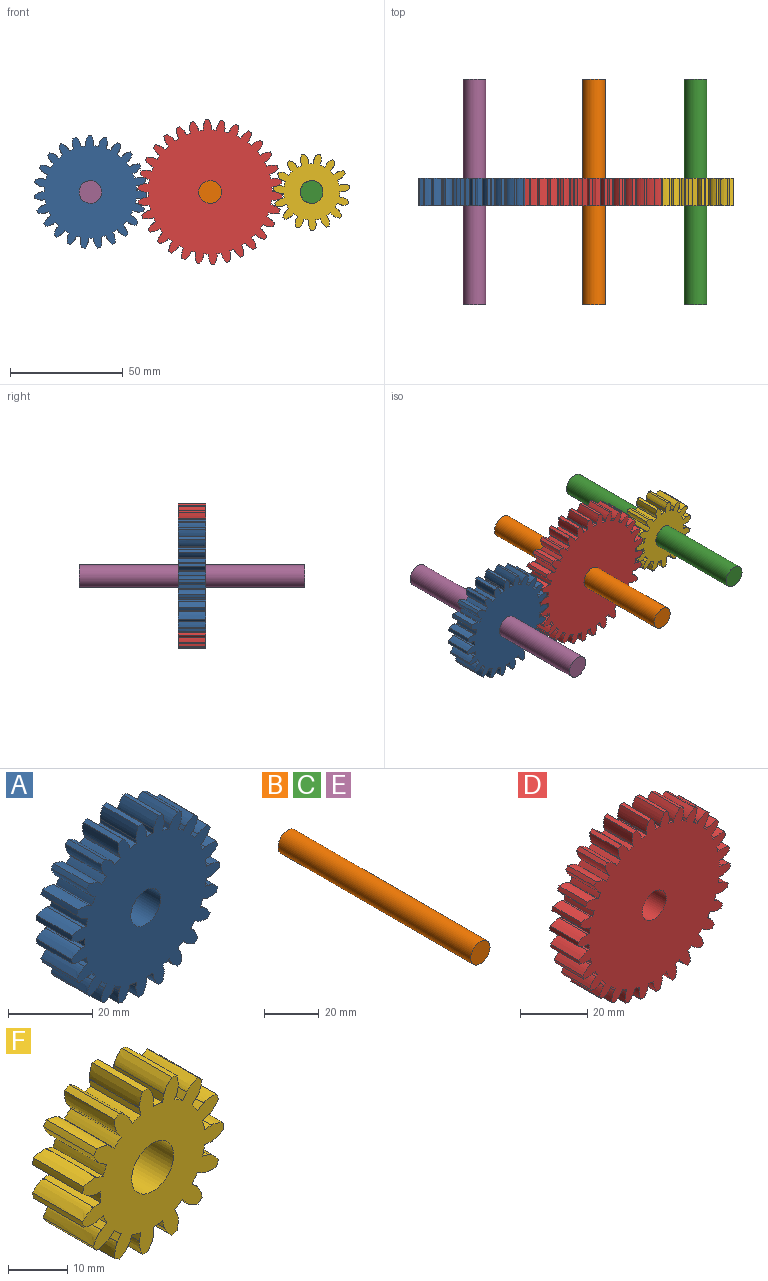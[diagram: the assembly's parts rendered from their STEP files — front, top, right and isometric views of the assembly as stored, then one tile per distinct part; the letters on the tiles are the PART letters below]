
ASSEMBLY  parts=6 mates=6
PART A: 141 faces, bbox 49.9x12x50 mm
  f0: cylinder r=20.5mm len=12mm, axis (0,1,0), area 25.9mm2, adj f23,f24,f26,f137
  f1: cylinder r=20.5mm len=12mm, axis (0,1,0), area 25.9mm2, adj f23,f24,f132,f136
  f2: cylinder r=20.5mm len=12mm, axis (0,1,0), area 25.9mm2, adj f23,f24,f127,f131
  f3: cylinder r=20.5mm len=12mm, axis (0,1,0), area 25.9mm2, adj f23,f24,f122,f126
  f4: cylinder r=20.5mm len=12mm, axis (0,1,0), area 25.9mm2, adj f23,f24,f117,f121
  f5: cylinder r=20.5mm len=12mm, axis (0,1,0), area 25.9mm2, adj f23,f24,f112,f116
  f6: cylinder r=20.5mm len=12mm, axis (0,1,0), area 25.9mm2, adj f23,f24,f107,f111
  f7: cylinder r=20.5mm len=12mm, axis (0,1,0), area 25.9mm2, adj f23,f24,f102,f106
  f8: cylinder r=20.5mm len=12mm, axis (0,1,0), area 25.9mm2, adj f23,f24,f97,f101
  f9: cylinder r=20.5mm len=12mm, axis (0,1,0), area 25.9mm2, adj f23,f24,f92,f96
  f10: cylinder r=20.5mm len=12mm, axis (0,1,0), area 25.9mm2, adj f23,f24,f87,f91
  f11: cylinder r=20.5mm len=12mm, axis (0,1,0), area 25.9mm2, adj f23,f24,f82,f86
  f12: cylinder r=20.5mm len=12mm, axis (0,1,0), area 25.9mm2, adj f23,f24,f77,f81
  f13: cylinder r=20.5mm len=12mm, axis (0,1,0), area 25.9mm2, adj f23,f24,f72,f76
  f14: cylinder r=20.5mm len=12mm, axis (0,1,0), area 25.9mm2, adj f23,f24,f67,f71
  f15: cylinder r=20.5mm len=12mm, axis (0,1,0), area 25.9mm2, adj f23,f24,f62,f66
  f16: cylinder r=20.5mm len=12mm, axis (0,1,0), area 25.9mm2, adj f23,f24,f57,f61
  f17: cylinder r=20.5mm len=12mm, axis (0,1,0), area 25.9mm2, adj f23,f24,f52,f56
  f18: cylinder r=20.5mm len=12mm, axis (0,1,0), area 25.9mm2, adj f23,f24,f47,f51
  f19: cylinder r=20.5mm len=12mm, axis (0,1,0), area 25.9mm2, adj f23,f24,f42,f46
  f20: cylinder r=20.5mm len=12mm, axis (0,1,0), area 25.9mm2, adj f23,f24,f37,f41
  f21: cylinder r=20.5mm len=12mm, axis (0,1,0), area 25.9mm2, adj f23,f24,f32,f36
  f22: cylinder r=20.5mm len=12mm, axis (0,1,0), area 25.9mm2, adj f23,f24,f27,f31
  f23: plane 49.96x49.85mm, normal (0,-1,0), area 1550.3mm2, adj f0,f1,f2,f3,f4,f5,f6,f7
  f24: plane 49.96x49.85mm, normal (0,1,0), area 1550.3mm2, adj f0,f1,f2,f3,f4,f5,f6,f7
  f25: extruded ~12x3.52mm, area 43.8mm2, adj f23,f24,f26,f29
  f26: plane 12x1.1mm, normal (-0.99,0,-0.14), area 13.4mm2, adj f0,f23,f24,f25
  f27: plane 12x1.11mm, normal (1,0,0), area 13.4mm2, adj f22,f23,f24,f28
  f28: extruded ~12x3.37mm, area 43.8mm2, adj f23,f24,f27,f29
  f29: cylinder r=25mm len=12mm, axis (0,1,0), area 17.1mm2, adj f23,f24,f25,f28
  f30: extruded ~12x3.16mm, area 43.8mm2, adj f23,f24,f31,f34
  f31: plane 12x1.1mm, normal (-0.99,0,0.14), area 13.4mm2, adj f22,f23,f24,f30
  f32: plane 12x1.07mm, normal (0.96,0,-0.27), area 13.4mm2, adj f21,f23,f24,f33
  f33: extruded ~12x3.6mm, area 43.8mm2, adj f23,f24,f32,f34
  f34: cylinder r=25mm len=12mm, axis (0,1,0), area 17.1mm2, adj f23,f24,f30,f33
  f35: extruded ~12x2.57mm, area 43.8mm2, adj f23,f24,f36,f39
  f36: plane 12x1.02mm, normal (-0.92,0,0.4), area 13.4mm2, adj f21,f23,f24,f35
  f37: plane 12x0.95mm, normal (0.85,0,-0.52), area 13.4mm2, adj f20,f23,f24,f38
  f38: extruded ~12x3.56mm, area 43.8mm2, adj f23,f24,f37,f39
  f39: cylinder r=25mm len=12mm, axis (0,1,0), area 17.1mm2, adj f23,f24,f35,f38
  f40: extruded ~12x3.15mm, area 43.8mm2, adj f23,f24,f41,f44
  f41: plane 12x0.86mm, normal (-0.78,0,0.63), area 13.4mm2, adj f20,f23,f24,f40
  f42: plane 12x0.81mm, normal (0.68,0,-0.73), area 13.4mm2, adj f19,f23,f24,f43
  f43: extruded ~12x3.26mm, area 43.8mm2, adj f23,f24,f42,f44
  f44: cylinder r=25mm len=12mm, axis (0,1,0), area 17.1mm2, adj f23,f24,f40,f43
  f45: extruded ~12x3.51mm, area 43.8mm2, adj f23,f24,f46,f49
  f46: plane 12x0.91mm, normal (-0.58,0,0.82), area 13.4mm2, adj f19,f23,f24,f45
  f47: plane 12x0.99mm, normal (0.46,0,-0.89), area 13.4mm2, adj f18,f23,f24,f48
  f48: extruded ~12x2.72mm, area 43.8mm2, adj f23,f24,f47,f49
  f49: cylinder r=25mm len=12mm, axis (0,1,0), area 17.1mm2, adj f23,f24,f45,f48
  f50: extruded ~12x3.62mm, area 43.8mm2, adj f23,f24,f51,f54
  f51: plane 12x1.05mm, normal (-0.33,0,0.94), area 13.4mm2, adj f18,f23,f24,f50
  f52: plane 12x1.09mm, normal (0.2,0,-0.98), area 13.4mm2, adj f17,f23,f24,f53
  f53: extruded ~12x3.03mm, area 43.8mm2, adj f23,f24,f52,f54
  f54: cylinder r=25mm len=12mm, axis (0,1,0), area 17.1mm2, adj f23,f24,f50,f53
  f55: extruded ~12x3.45mm, area 43.8mm2, adj f23,f24,f56,f59
  f56: plane 12x1.11mm, normal (-0.07,0,1), area 13.4mm2, adj f17,f23,f24,f55
  f57: plane 12x1.11mm, normal (-0.07,0,-1), area 13.4mm2, adj f16,f23,f24,f58
  f58: extruded ~12x3.45mm, area 43.8mm2, adj f23,f24,f57,f59
  f59: cylinder r=25mm len=12mm, axis (0,1,0), area 17.1mm2, adj f23,f24,f55,f58
  f60: extruded ~12x3.03mm, area 43.8mm2, adj f23,f24,f61,f64
  f61: plane 12x1.09mm, normal (0.2,0,0.98), area 13.4mm2, adj f16,f23,f24,f60
  f62: plane 12x1.05mm, normal (-0.33,0,-0.94), area 13.4mm2, adj f15,f23,f24,f63
  f63: extruded ~12x3.62mm, area 43.8mm2, adj f23,f24,f62,f64
  f64: cylinder r=25mm len=12mm, axis (0,1,0), area 17.1mm2, adj f23,f24,f60,f63
  f65: extruded ~12x2.72mm, area 43.8mm2, adj f23,f24,f66,f69
  f66: plane 12x0.99mm, normal (0.46,0,0.89), area 13.4mm2, adj f15,f23,f24,f65
  f67: plane 12x0.91mm, normal (-0.58,0,-0.82), area 13.4mm2, adj f14,f23,f24,f68
  f68: extruded ~12x3.51mm, area 43.8mm2, adj f23,f24,f67,f69
  f69: cylinder r=25mm len=12mm, axis (0,1,0), area 17.1mm2, adj f23,f24,f65,f68
  f70: extruded ~12x3.26mm, area 43.8mm2, adj f23,f24,f71,f74
  f71: plane 12x0.81mm, normal (0.68,0,0.73), area 13.4mm2, adj f14,f23,f24,f70
  f72: plane 12x0.86mm, normal (-0.78,0,-0.63), area 13.4mm2, adj f13,f23,f24,f73
  f73: extruded ~12x3.15mm, area 43.8mm2, adj f23,f24,f72,f74
  f74: cylinder r=25mm len=12mm, axis (0,1,0), area 17.1mm2, adj f23,f24,f70,f73
  f75: extruded ~12x3.56mm, area 43.8mm2, adj f23,f24,f76,f79
  f76: plane 12x0.95mm, normal (0.85,0,0.52), area 13.4mm2, adj f13,f23,f24,f75
  f77: plane 12x1.02mm, normal (-0.92,0,-0.4), area 13.4mm2, adj f12,f23,f24,f78
  f78: extruded ~12x2.57mm, area 43.8mm2, adj f23,f24,f77,f79
  f79: cylinder r=25mm len=12mm, axis (0,1,0), area 17.1mm2, adj f23,f24,f75,f78
  f80: extruded ~12x3.6mm, area 43.8mm2, adj f23,f24,f81,f84
  f81: plane 12x1.07mm, normal (0.96,0,0.27), area 13.4mm2, adj f12,f23,f24,f80
  f82: plane 12x1.1mm, normal (-0.99,0,-0.14), area 13.4mm2, adj f11,f23,f24,f83
  f83: extruded ~12x3.16mm, area 43.8mm2, adj f23,f24,f82,f84
  f84: cylinder r=25mm len=12mm, axis (0,1,0), area 17.1mm2, adj f23,f24,f80,f83
  f85: extruded ~12x3.37mm, area 43.8mm2, adj f23,f24,f86,f89
  f86: plane 12x1.11mm, normal (1,0,0), area 13.4mm2, adj f11,f23,f24,f85
  f87: plane 12x1.1mm, normal (-0.99,0,0.14), area 13.4mm2, adj f10,f23,f24,f88
  f88: extruded ~12x3.52mm, area 43.8mm2, adj f23,f24,f87,f89
  f89: cylinder r=25mm len=12mm, axis (0,1,0), area 17.1mm2, adj f23,f24,f85,f88
  f90: extruded ~12x2.89mm, area 43.8mm2, adj f23,f24,f91,f94
  f91: plane 12x1.07mm, normal (0.96,0,-0.27), area 13.4mm2, adj f10,f23,f24,f90
  f92: plane 12x1.02mm, normal (-0.92,0,0.4), area 13.4mm2, adj f9,f23,f24,f93
  f93: extruded ~12x3.62mm, area 43.8mm2, adj f23,f24,f92,f94
  f94: cylinder r=25mm len=12mm, axis (0,1,0), area 17.1mm2, adj f23,f24,f90,f93
  f95: extruded ~12x2.88mm, area 43.8mm2, adj f23,f24,f96,f99
  f96: plane 12x0.95mm, normal (0.85,0,-0.52), area 13.4mm2, adj f9,f23,f24,f95
  f97: plane 12x0.86mm, normal (-0.78,0,0.63), area 13.4mm2, adj f8,f23,f24,f98
  f98: extruded ~12x3.45mm, area 43.8mm2, adj f23,f24,f97,f99
  f99: cylinder r=25mm len=12mm, axis (0,1,0), area 17.1mm2, adj f23,f24,f95,f98
  f100: extruded ~12x3.36mm, area 43.8mm2, adj f23,f24,f101,f104
  f101: plane 12x0.81mm, normal (0.68,0,-0.73), area 13.4mm2, adj f8,f23,f24,f100
  f102: plane 12x0.91mm, normal (-0.58,0,0.82), area 13.4mm2, adj f7,f23,f24,f103
  f103: extruded ~12x3.02mm, area 43.8mm2, adj f23,f24,f102,f104
  f104: cylinder r=25mm len=12mm, axis (0,1,0), area 17.1mm2, adj f23,f24,f100,f103
  f105: extruded ~12x3.6mm, area 43.8mm2, adj f23,f24,f106,f109
  f106: plane 12x0.99mm, normal (0.46,0,-0.89), area 13.4mm2, adj f7,f23,f24,f105
  f107: plane 12x1.05mm, normal (-0.33,0,0.94), area 13.4mm2, adj f6,f23,f24,f108
  f108: extruded ~12x2.73mm, area 43.8mm2, adj f23,f24,f107,f109
  f109: cylinder r=25mm len=12mm, axis (0,1,0), area 17.1mm2, adj f23,f24,f105,f108
  f110: extruded ~12x3.57mm, area 43.8mm2, adj f23,f24,f111,f114
  f111: plane 12x1.09mm, normal (0.2,0,-0.98), area 13.4mm2, adj f6,f23,f24,f110
  f112: plane 12x1.11mm, normal (-0.07,0,1), area 13.4mm2, adj f5,f23,f24,f113
  f113: extruded ~12x3.27mm, area 43.8mm2, adj f23,f24,f112,f114
  f114: cylinder r=25mm len=12mm, axis (0,1,0), area 17.1mm2, adj f23,f24,f110,f113
  f115: extruded ~12x3.27mm, area 43.8mm2, adj f23,f24,f116,f119
  f116: plane 12x1.11mm, normal (-0.07,0,-1), area 13.4mm2, adj f5,f23,f24,f115
  f117: plane 12x1.09mm, normal (0.2,0,0.98), area 13.4mm2, adj f4,f23,f24,f118
  f118: extruded ~12x3.57mm, area 43.8mm2, adj f23,f24,f117,f119
  f119: cylinder r=25mm len=12mm, axis (0,1,0), area 17.1mm2, adj f23,f24,f115,f118
  f120: extruded ~12x2.73mm, area 43.8mm2, adj f23,f24,f121,f124
  f121: plane 12x1.05mm, normal (-0.33,0,-0.94), area 13.4mm2, adj f4,f23,f24,f120
  f122: plane 12x0.99mm, normal (0.46,0,0.89), area 13.4mm2, adj f3,f23,f24,f123
  f123: extruded ~12x3.6mm, area 43.8mm2, adj f23,f24,f122,f124
  f124: cylinder r=25mm len=12mm, axis (0,1,0), area 17.1mm2, adj f23,f24,f120,f123
  f125: extruded ~12x3.02mm, area 43.8mm2, adj f23,f24,f126,f129
  f126: plane 12x0.91mm, normal (-0.58,0,-0.82), area 13.4mm2, adj f3,f23,f24,f125
  f127: plane 12x0.81mm, normal (0.68,0,0.73), area 13.4mm2, adj f2,f23,f24,f128
  f128: extruded ~12x3.36mm, area 43.8mm2, adj f23,f24,f127,f129
  f129: cylinder r=25mm len=12mm, axis (0,1,0), area 17.1mm2, adj f23,f24,f125,f128
  f130: extruded ~12x3.45mm, area 43.8mm2, adj f23,f24,f131,f134
  f131: plane 12x0.86mm, normal (-0.78,0,-0.63), area 13.4mm2, adj f2,f23,f24,f130
  f132: plane 12x0.95mm, normal (0.85,0,0.52), area 13.4mm2, adj f1,f23,f24,f133
  f133: extruded ~12x2.88mm, area 43.8mm2, adj f23,f24,f132,f134
  f134: cylinder r=25mm len=12mm, axis (0,1,0), area 17.1mm2, adj f23,f24,f130,f133
  f135: extruded ~12x3.62mm, area 43.8mm2, adj f23,f24,f136,f139
  f136: plane 12x1.02mm, normal (-0.92,0,-0.4), area 13.4mm2, adj f1,f23,f24,f135
  f137: plane 12x1.07mm, normal (0.96,0,0.27), area 13.4mm2, adj f0,f23,f24,f138
  f138: extruded ~12x2.89mm, area 43.8mm2, adj f23,f24,f137,f139
  f139: cylinder r=25mm len=12mm, axis (0,1,0), area 17.1mm2, adj f23,f24,f135,f138
  f140: cylinder r=5mm len=12mm, axis (0,1,0), area 377mm2, adj f23,f24
PART B: 3 faces, bbox 10x100x10 mm
  f0: cylinder r=5mm len=100mm, axis (0,1,0), area 3141.6mm2, adj f1,f2
  f1: plane 10x10mm, normal (0,-1,0), area 78.5mm2, adj f0
  f2: plane 10x10mm, normal (0,1,0), area 78.5mm2, adj f0
PART C: same geometry as B
PART D: 183 faces, bbox 64x12x64 mm
  f0: cylinder r=27.5mm len=12mm, axis (0,1,0), area 24.5mm2, adj f30,f31,f33,f179
  f1: cylinder r=27.5mm len=12mm, axis (0,1,0), area 24.5mm2, adj f30,f31,f174,f178
  f2: cylinder r=27.5mm len=12mm, axis (0,1,0), area 24.5mm2, adj f30,f31,f169,f173
  f3: cylinder r=27.5mm len=12mm, axis (0,1,0), area 24.5mm2, adj f30,f31,f164,f168
  f4: cylinder r=27.5mm len=12mm, axis (0,1,0), area 24.5mm2, adj f30,f31,f159,f163
  f5: cylinder r=27.5mm len=12mm, axis (0,1,0), area 24.5mm2, adj f30,f31,f154,f158
  f6: cylinder r=27.5mm len=12mm, axis (0,1,0), area 24.5mm2, adj f30,f31,f149,f153
  f7: cylinder r=27.5mm len=12mm, axis (0,1,0), area 24.5mm2, adj f30,f31,f144,f148
  f8: cylinder r=27.5mm len=12mm, axis (0,1,0), area 24.5mm2, adj f30,f31,f139,f143
  f9: cylinder r=27.5mm len=12mm, axis (0,1,0), area 24.5mm2, adj f30,f31,f134,f138
  f10: cylinder r=27.5mm len=12mm, axis (0,1,0), area 24.5mm2, adj f30,f31,f129,f133
  f11: cylinder r=27.5mm len=12mm, axis (0,1,0), area 24.5mm2, adj f30,f31,f124,f128
  f12: cylinder r=27.5mm len=12mm, axis (0,1,0), area 24.5mm2, adj f30,f31,f119,f123
  f13: cylinder r=27.5mm len=12mm, axis (0,1,0), area 24.5mm2, adj f30,f31,f114,f118
  f14: cylinder r=27.5mm len=12mm, axis (0,1,0), area 24.5mm2, adj f30,f31,f109,f113
  f15: cylinder r=27.5mm len=12mm, axis (0,1,0), area 24.5mm2, adj f30,f31,f104,f108
  f16: cylinder r=27.5mm len=12mm, axis (0,1,0), area 24.5mm2, adj f30,f31,f99,f103
  f17: cylinder r=27.5mm len=12mm, axis (0,1,0), area 24.5mm2, adj f30,f31,f94,f98
  f18: cylinder r=27.5mm len=12mm, axis (0,1,0), area 24.5mm2, adj f30,f31,f89,f93
  f19: cylinder r=27.5mm len=12mm, axis (0,1,0), area 24.5mm2, adj f30,f31,f84,f88
  f20: cylinder r=27.5mm len=12mm, axis (0,1,0), area 24.5mm2, adj f30,f31,f79,f83
  f21: cylinder r=27.5mm len=12mm, axis (0,1,0), area 24.5mm2, adj f30,f31,f74,f78
  f22: cylinder r=27.5mm len=12mm, axis (0,1,0), area 24.5mm2, adj f30,f31,f69,f73
  f23: cylinder r=27.5mm len=12mm, axis (0,1,0), area 24.5mm2, adj f30,f31,f64,f68
  f24: cylinder r=27.5mm len=12mm, axis (0,1,0), area 24.5mm2, adj f30,f31,f59,f63
  f25: cylinder r=27.5mm len=12mm, axis (0,1,0), area 24.5mm2, adj f30,f31,f54,f58
  f26: cylinder r=27.5mm len=12mm, axis (0,1,0), area 24.5mm2, adj f30,f31,f49,f53
  f27: cylinder r=27.5mm len=12mm, axis (0,1,0), area 24.5mm2, adj f30,f31,f44,f48
  f28: cylinder r=27.5mm len=12mm, axis (0,1,0), area 24.5mm2, adj f30,f31,f39,f43
  f29: cylinder r=27.5mm len=12mm, axis (0,1,0), area 24.5mm2, adj f30,f31,f34,f38
  f30: plane 63.97x63.97mm, normal (0,-1,0), area 2710.6mm2, adj f0,f1,f2,f3,f4,f5,f6,f7
  f31: plane 63.97x63.97mm, normal (0,1,0), area 2710.6mm2, adj f0,f1,f2,f3,f4,f5,f6,f7
  f32: extruded ~12x3.92mm, area 48.8mm2, adj f30,f31,f33,f36
  f33: plane 12x0.69mm, normal (-0.99,0,-0.1), area 8.3mm2, adj f0,f30,f31,f32
  f34: plane 12x0.69mm, normal (1,0,0), area 8.3mm2, adj f29,f30,f31,f35
  f35: extruded ~12x3.8mm, area 48.8mm2, adj f30,f31,f34,f36
  f36: cylinder r=32mm len=12mm, axis (0,1,0), area 17.7mm2, adj f30,f31,f32,f35
  f37: extruded ~12x3.64mm, area 48.8mm2, adj f30,f31,f38,f41
  f38: plane 12x0.69mm, normal (-0.99,0,0.1), area 8.3mm2, adj f29,f30,f31,f37
  f39: plane 12x0.68mm, normal (0.98,0,-0.21), area 8.3mm2, adj f28,f30,f31,f40
  f40: extruded ~12x4mm, area 48.8mm2, adj f30,f31,f39,f41
  f41: cylinder r=32mm len=12mm, axis (0,1,0), area 17.7mm2, adj f30,f31,f37,f40
  f42: extruded ~12x3.19mm, area 48.8mm2, adj f30,f31,f43,f46
  f43: plane 12x0.66mm, normal (-0.95,0,0.31), area 8.3mm2, adj f28,f30,f31,f42
  f44: plane 12x0.63mm, normal (0.91,0,-0.41), area 8.3mm2, adj f27,f30,f31,f45
  f45: extruded ~12x4.02mm, area 48.8mm2, adj f30,f31,f44,f46
  f46: cylinder r=32mm len=12mm, axis (0,1,0), area 17.7mm2, adj f30,f31,f42,f45
  f47: extruded ~12x3.08mm, area 48.8mm2, adj f30,f31,f48,f51
  f48: plane 12x0.6mm, normal (-0.87,0,0.5), area 8.3mm2, adj f27,f30,f31,f47
  f49: plane 12x0.56mm, normal (0.81,0,-0.59), area 8.3mm2, adj f26,f30,f31,f50
  f50: extruded ~12x3.87mm, area 48.8mm2, adj f30,f31,f49,f51
  f51: cylinder r=32mm len=12mm, axis (0,1,0), area 17.7mm2, adj f30,f31,f47,f50
  f52: extruded ~12x3.55mm, area 48.8mm2, adj f30,f31,f53,f56
  f53: plane 12x0.51mm, normal (-0.74,0,0.67), area 8.3mm2, adj f26,f30,f31,f52
  f54: plane 12x0.51mm, normal (0.67,0,-0.74), area 8.3mm2, adj f25,f30,f31,f55
  f55: extruded ~12x3.55mm, area 48.8mm2, adj f30,f31,f54,f56
  f56: cylinder r=32mm len=12mm, axis (0,1,0), area 17.7mm2, adj f30,f31,f52,f55
  f57: extruded ~12x3.87mm, area 48.8mm2, adj f30,f31,f58,f61
  f58: plane 12x0.56mm, normal (-0.59,0,0.81), area 8.3mm2, adj f25,f30,f31,f57
  f59: plane 12x0.6mm, normal (0.5,0,-0.87), area 8.3mm2, adj f24,f30,f31,f60
  f60: extruded ~12x3.08mm, area 48.8mm2, adj f30,f31,f59,f61
  f61: cylinder r=32mm len=12mm, axis (0,1,0), area 17.7mm2, adj f30,f31,f57,f60
  f62: extruded ~12x4.02mm, area 48.8mm2, adj f30,f31,f63,f66
  f63: plane 12x0.63mm, normal (-0.41,0,0.91), area 8.3mm2, adj f24,f30,f31,f62
  f64: plane 12x0.66mm, normal (0.31,0,-0.95), area 8.3mm2, adj f23,f30,f31,f65
  f65: extruded ~12x3.19mm, area 48.8mm2, adj f30,f31,f64,f66
  f66: cylinder r=32mm len=12mm, axis (0,1,0), area 17.7mm2, adj f30,f31,f62,f65
  f67: extruded ~12x4mm, area 48.8mm2, adj f30,f31,f68,f71
  f68: plane 12x0.68mm, normal (-0.21,0,0.98), area 8.3mm2, adj f23,f30,f31,f67
  f69: plane 12x0.69mm, normal (0.1,0,-0.99), area 8.3mm2, adj f22,f30,f31,f70
  f70: extruded ~12x3.64mm, area 48.8mm2, adj f30,f31,f69,f71
  f71: cylinder r=32mm len=12mm, axis (0,1,0), area 17.7mm2, adj f30,f31,f67,f70
  f72: extruded ~12x3.8mm, area 48.8mm2, adj f30,f31,f73,f76
  f73: plane 12x0.69mm, normal (0,0,1), area 8.3mm2, adj f22,f30,f31,f72
  f74: plane 12x0.69mm, normal (-0.1,0,-0.99), area 8.3mm2, adj f21,f30,f31,f75
  f75: extruded ~12x3.92mm, area 48.8mm2, adj f30,f31,f74,f76
  f76: cylinder r=32mm len=12mm, axis (0,1,0), area 17.7mm2, adj f30,f31,f72,f75
  f77: extruded ~12x3.43mm, area 48.8mm2, adj f30,f31,f78,f81
  f78: plane 12x0.68mm, normal (0.21,0,0.98), area 8.3mm2, adj f21,f30,f31,f77
  f79: plane 12x0.66mm, normal (-0.31,0,-0.95), area 8.3mm2, adj f20,f30,f31,f80
  f80: extruded ~12x4.03mm, area 48.8mm2, adj f30,f31,f79,f81
  f81: cylinder r=32mm len=12mm, axis (0,1,0), area 17.7mm2, adj f30,f31,f77,f80
  f82: extruded ~12x2.92mm, area 48.8mm2, adj f30,f31,f83,f86
  f83: plane 12x0.63mm, normal (0.41,0,0.91), area 8.3mm2, adj f20,f30,f31,f82
  f84: plane 12x0.6mm, normal (-0.5,0,-0.87), area 8.3mm2, adj f19,f30,f31,f85
  f85: extruded ~12x3.97mm, area 48.8mm2, adj f30,f31,f84,f86
  f86: cylinder r=32mm len=12mm, axis (0,1,0), area 17.7mm2, adj f30,f31,f82,f85
  f87: extruded ~12x3.33mm, area 48.8mm2, adj f30,f31,f88,f91
  f88: plane 12x0.56mm, normal (0.59,0,0.81), area 8.3mm2, adj f19,f30,f31,f87
  f89: plane 12x0.51mm, normal (-0.67,0,-0.74), area 8.3mm2, adj f18,f30,f31,f90
  f90: extruded ~12x3.73mm, area 48.8mm2, adj f30,f31,f89,f91
  f91: cylinder r=32mm len=12mm, axis (0,1,0), area 17.7mm2, adj f30,f31,f87,f90
  f92: extruded ~12x3.73mm, area 48.8mm2, adj f30,f31,f93,f96
  f93: plane 12x0.51mm, normal (0.74,0,0.67), area 8.3mm2, adj f18,f30,f31,f92
  f94: plane 12x0.56mm, normal (-0.81,0,-0.59), area 8.3mm2, adj f17,f30,f31,f95
  f95: extruded ~12x3.33mm, area 48.8mm2, adj f30,f31,f94,f96
  f96: cylinder r=32mm len=12mm, axis (0,1,0), area 17.7mm2, adj f30,f31,f92,f95
  f97: extruded ~12x3.97mm, area 48.8mm2, adj f30,f31,f98,f101
  f98: plane 12x0.6mm, normal (0.87,0,0.5), area 8.3mm2, adj f17,f30,f31,f97
  f99: plane 12x0.63mm, normal (-0.91,0,-0.41), area 8.3mm2, adj f16,f30,f31,f100
  f100: extruded ~12x2.92mm, area 48.8mm2, adj f30,f31,f99,f101
  f101: cylinder r=32mm len=12mm, axis (0,1,0), area 17.7mm2, adj f30,f31,f97,f100
  f102: extruded ~12x4.03mm, area 48.8mm2, adj f30,f31,f103,f106
  f103: plane 12x0.66mm, normal (0.95,0,0.31), area 8.3mm2, adj f16,f30,f31,f102
  f104: plane 12x0.68mm, normal (-0.98,0,-0.21), area 8.3mm2, adj f15,f30,f31,f105
  f105: extruded ~12x3.43mm, area 48.8mm2, adj f30,f31,f104,f106
  f106: cylinder r=32mm len=12mm, axis (0,1,0), area 17.7mm2, adj f30,f31,f102,f105
  f107: extruded ~12x3.92mm, area 48.8mm2, adj f30,f31,f108,f111
  f108: plane 12x0.69mm, normal (0.99,0,0.1), area 8.3mm2, adj f15,f30,f31,f107
  f109: plane 12x0.69mm, normal (-1,0,0), area 8.3mm2, adj f14,f30,f31,f110
  f110: extruded ~12x3.8mm, area 48.8mm2, adj f30,f31,f109,f111
  f111: cylinder r=32mm len=12mm, axis (0,1,0), area 17.7mm2, adj f30,f31,f107,f110
  f112: extruded ~12x3.64mm, area 48.8mm2, adj f30,f31,f113,f116
  f113: plane 12x0.69mm, normal (0.99,0,-0.1), area 8.3mm2, adj f14,f30,f31,f112
  f114: plane 12x0.68mm, normal (-0.98,0,0.21), area 8.3mm2, adj f13,f30,f31,f115
  f115: extruded ~12x4mm, area 48.8mm2, adj f30,f31,f114,f116
  f116: cylinder r=32mm len=12mm, axis (0,1,0), area 17.7mm2, adj f30,f31,f112,f115
  f117: extruded ~12x3.19mm, area 48.8mm2, adj f30,f31,f118,f121
  f118: plane 12x0.66mm, normal (0.95,0,-0.31), area 8.3mm2, adj f13,f30,f31,f117
  f119: plane 12x0.63mm, normal (-0.91,0,0.41), area 8.3mm2, adj f12,f30,f31,f120
  f120: extruded ~12x4.02mm, area 48.8mm2, adj f30,f31,f119,f121
  f121: cylinder r=32mm len=12mm, axis (0,1,0), area 17.7mm2, adj f30,f31,f117,f120
  f122: extruded ~12x3.08mm, area 48.8mm2, adj f30,f31,f123,f126
  f123: plane 12x0.6mm, normal (0.87,0,-0.5), area 8.3mm2, adj f12,f30,f31,f122
  f124: plane 12x0.56mm, normal (-0.81,0,0.59), area 8.3mm2, adj f11,f30,f31,f125
  f125: extruded ~12x3.87mm, area 48.8mm2, adj f30,f31,f124,f126
  f126: cylinder r=32mm len=12mm, axis (0,1,0), area 17.7mm2, adj f30,f31,f122,f125
  f127: extruded ~12x3.55mm, area 48.8mm2, adj f30,f31,f128,f131
  f128: plane 12x0.51mm, normal (0.74,0,-0.67), area 8.3mm2, adj f11,f30,f31,f127
  f129: plane 12x0.51mm, normal (-0.67,0,0.74), area 8.3mm2, adj f10,f30,f31,f130
  f130: extruded ~12x3.55mm, area 48.8mm2, adj f30,f31,f129,f131
  f131: cylinder r=32mm len=12mm, axis (0,1,0), area 17.7mm2, adj f30,f31,f127,f130
  f132: extruded ~12x3.87mm, area 48.8mm2, adj f30,f31,f133,f136
  f133: plane 12x0.56mm, normal (0.59,0,-0.81), area 8.3mm2, adj f10,f30,f31,f132
  f134: plane 12x0.6mm, normal (-0.5,0,0.87), area 8.3mm2, adj f9,f30,f31,f135
  f135: extruded ~12x3.08mm, area 48.8mm2, adj f30,f31,f134,f136
  f136: cylinder r=32mm len=12mm, axis (0,1,0), area 17.7mm2, adj f30,f31,f132,f135
  f137: extruded ~12x4.02mm, area 48.8mm2, adj f30,f31,f138,f141
  f138: plane 12x0.63mm, normal (0.41,0,-0.91), area 8.3mm2, adj f9,f30,f31,f137
  f139: plane 12x0.66mm, normal (-0.31,0,0.95), area 8.3mm2, adj f8,f30,f31,f140
  f140: extruded ~12x3.19mm, area 48.8mm2, adj f30,f31,f139,f141
  f141: cylinder r=32mm len=12mm, axis (0,1,0), area 17.7mm2, adj f30,f31,f137,f140
  f142: extruded ~12x4mm, area 48.8mm2, adj f30,f31,f143,f146
  f143: plane 12x0.68mm, normal (0.21,0,-0.98), area 8.3mm2, adj f8,f30,f31,f142
  f144: plane 12x0.69mm, normal (-0.1,0,0.99), area 8.3mm2, adj f7,f30,f31,f145
  f145: extruded ~12x3.64mm, area 48.8mm2, adj f30,f31,f144,f146
  f146: cylinder r=32mm len=12mm, axis (0,1,0), area 17.7mm2, adj f30,f31,f142,f145
  f147: extruded ~12x3.8mm, area 48.8mm2, adj f30,f31,f148,f151
  f148: plane 12x0.69mm, normal (0,0,-1), area 8.3mm2, adj f7,f30,f31,f147
  f149: plane 12x0.69mm, normal (0.1,0,0.99), area 8.3mm2, adj f6,f30,f31,f150
  f150: extruded ~12x3.92mm, area 48.8mm2, adj f30,f31,f149,f151
  f151: cylinder r=32mm len=12mm, axis (0,1,0), area 17.7mm2, adj f30,f31,f147,f150
  f152: extruded ~12x3.43mm, area 48.8mm2, adj f30,f31,f153,f156
  f153: plane 12x0.68mm, normal (-0.21,0,-0.98), area 8.3mm2, adj f6,f30,f31,f152
  f154: plane 12x0.66mm, normal (0.31,0,0.95), area 8.3mm2, adj f5,f30,f31,f155
  f155: extruded ~12x4.03mm, area 48.8mm2, adj f30,f31,f154,f156
  f156: cylinder r=32mm len=12mm, axis (0,1,0), area 17.7mm2, adj f30,f31,f152,f155
  f157: extruded ~12x2.92mm, area 48.8mm2, adj f30,f31,f158,f161
  f158: plane 12x0.63mm, normal (-0.41,0,-0.91), area 8.3mm2, adj f5,f30,f31,f157
  f159: plane 12x0.6mm, normal (0.5,0,0.87), area 8.3mm2, adj f4,f30,f31,f160
  f160: extruded ~12x3.97mm, area 48.8mm2, adj f30,f31,f159,f161
  f161: cylinder r=32mm len=12mm, axis (0,1,0), area 17.7mm2, adj f30,f31,f157,f160
  f162: extruded ~12x3.33mm, area 48.8mm2, adj f30,f31,f163,f166
  f163: plane 12x0.56mm, normal (-0.59,0,-0.81), area 8.3mm2, adj f4,f30,f31,f162
  f164: plane 12x0.51mm, normal (0.67,0,0.74), area 8.3mm2, adj f3,f30,f31,f165
  f165: extruded ~12x3.73mm, area 48.8mm2, adj f30,f31,f164,f166
  f166: cylinder r=32mm len=12mm, axis (0,1,0), area 17.7mm2, adj f30,f31,f162,f165
  f167: extruded ~12x3.73mm, area 48.8mm2, adj f30,f31,f168,f171
  f168: plane 12x0.51mm, normal (-0.74,0,-0.67), area 8.3mm2, adj f3,f30,f31,f167
  f169: plane 12x0.56mm, normal (0.81,0,0.59), area 8.3mm2, adj f2,f30,f31,f170
  f170: extruded ~12x3.33mm, area 48.8mm2, adj f30,f31,f169,f171
  f171: cylinder r=32mm len=12mm, axis (0,1,0), area 17.7mm2, adj f30,f31,f167,f170
  f172: extruded ~12x3.97mm, area 48.8mm2, adj f30,f31,f173,f176
  f173: plane 12x0.6mm, normal (-0.87,0,-0.5), area 8.3mm2, adj f2,f30,f31,f172
  f174: plane 12x0.63mm, normal (0.91,0,0.41), area 8.3mm2, adj f1,f30,f31,f175
  f175: extruded ~12x2.92mm, area 48.8mm2, adj f30,f31,f174,f176
  f176: cylinder r=32mm len=12mm, axis (0,1,0), area 17.7mm2, adj f30,f31,f172,f175
  f177: extruded ~12x4.03mm, area 48.8mm2, adj f30,f31,f178,f181
  f178: plane 12x0.66mm, normal (-0.95,0,-0.31), area 8.3mm2, adj f1,f30,f31,f177
  f179: plane 12x0.68mm, normal (0.98,0,0.21), area 8.3mm2, adj f0,f30,f31,f180
  f180: extruded ~12x3.43mm, area 48.8mm2, adj f30,f31,f179,f181
  f181: cylinder r=32mm len=12mm, axis (0,1,0), area 17.7mm2, adj f30,f31,f177,f180
  f182: cylinder r=5mm len=12mm, axis (0,1,0), area 377mm2, adj f30,f31
PART E: same geometry as B
PART F: 93 faces, bbox 33.8x12x33.9 mm
  f0: cylinder r=12.5mm len=12mm, axis (0,1,0), area 26.4mm2, adj f15,f16,f18,f89
  f1: cylinder r=12.5mm len=12mm, axis (0,1,0), area 26.4mm2, adj f15,f16,f84,f88
  f2: cylinder r=12.5mm len=12mm, axis (0,1,0), area 26.4mm2, adj f15,f16,f79,f83
  f3: cylinder r=12.5mm len=12mm, axis (0,1,0), area 26.4mm2, adj f15,f16,f74,f78
  f4: cylinder r=12.5mm len=12mm, axis (0,1,0), area 26.4mm2, adj f15,f16,f69,f73
  f5: cylinder r=12.5mm len=12mm, axis (0,1,0), area 26.4mm2, adj f15,f16,f64,f68
  f6: cylinder r=12.5mm len=12mm, axis (0,1,0), area 26.4mm2, adj f15,f16,f59,f63
  f7: cylinder r=12.5mm len=12mm, axis (0,1,0), area 26.4mm2, adj f15,f16,f54,f58
  f8: cylinder r=12.5mm len=12mm, axis (0,1,0), area 26.4mm2, adj f15,f16,f49,f53
  f9: cylinder r=12.5mm len=12mm, axis (0,1,0), area 26.4mm2, adj f15,f16,f44,f48
  f10: cylinder r=12.5mm len=12mm, axis (0,1,0), area 26.4mm2, adj f15,f16,f39,f43
  f11: cylinder r=12.5mm len=12mm, axis (0,1,0), area 26.4mm2, adj f15,f16,f34,f38
  f12: cylinder r=12.5mm len=12mm, axis (0,1,0), area 26.4mm2, adj f15,f16,f29,f33
  f13: cylinder r=12.5mm len=12mm, axis (0,1,0), area 26.4mm2, adj f15,f16,f24,f28
  f14: cylinder r=12.5mm len=12mm, axis (0,1,0), area 26.4mm2, adj f15,f16,f19,f23
  f15: plane 33.93x33.75mm, normal (0,-1,0), area 604.2mm2, adj f0,f1,f2,f3,f4,f5,f6,f7
  f16: plane 33.93x33.75mm, normal (0,1,0), area 604.2mm2, adj f0,f1,f2,f3,f4,f5,f6,f7
  f17: extruded ~12x3.08mm, area 38.6mm2, adj f15,f16,f18,f21
  f18: plane 12x1.56mm, normal (-0.98,0,-0.21), area 19.1mm2, adj f0,f15,f16,f17
  f19: plane 12x1.6mm, normal (1,0,0), area 19.1mm2, adj f14,f15,f16,f20
  f20: extruded ~12x2.87mm, area 38.6mm2, adj f15,f16,f19,f21
  f21: cylinder r=17mm len=12mm, axis (0,1,0), area 15.8mm2, adj f15,f16,f17,f20
  f22: extruded ~12x2.53mm, area 38.6mm2, adj f15,f16,f23,f26
  f23: plane 12x1.56mm, normal (-0.98,0,0.21), area 19.1mm2, adj f14,f15,f16,f22
  f24: plane 12x1.46mm, normal (0.91,0,-0.41), area 19.1mm2, adj f13,f15,f16,f25
  f25: extruded ~12x3.16mm, area 38.6mm2, adj f15,f16,f24,f26
  f26: cylinder r=17mm len=12mm, axis (0,1,0), area 15.8mm2, adj f15,f16,f22,f25
  f27: extruded ~12x2.77mm, area 38.6mm2, adj f15,f16,f28,f31
  f28: plane 12x1.29mm, normal (-0.81,0,0.59), area 19.1mm2, adj f13,f15,f16,f27
  f29: plane 12x1.19mm, normal (0.67,0,-0.74), area 19.1mm2, adj f12,f15,f16,f30
  f30: extruded ~12x2.91mm, area 38.6mm2, adj f15,f16,f29,f31
  f31: cylinder r=17mm len=12mm, axis (0,1,0), area 15.8mm2, adj f15,f16,f27,f30
  f32: extruded ~12x3.15mm, area 38.6mm2, adj f15,f16,f33,f36
  f33: plane 12x1.38mm, normal (-0.5,0,0.87), area 19.1mm2, adj f12,f15,f16,f32
  f34: plane 12x1.52mm, normal (0.31,0,-0.95), area 19.1mm2, adj f11,f15,f16,f35
  f35: extruded ~12x2.32mm, area 38.6mm2, adj f15,f16,f34,f36
  f36: cylinder r=17mm len=12mm, axis (0,1,0), area 15.8mm2, adj f15,f16,f32,f35
  f37: extruded ~12x2.99mm, area 38.6mm2, adj f15,f16,f38,f41
  f38: plane 12x1.59mm, normal (-0.1,0,0.99), area 19.1mm2, adj f11,f15,f16,f37
  f39: plane 12x1.59mm, normal (-0.1,0,-0.99), area 19.1mm2, adj f10,f15,f16,f40
  f40: extruded ~12x2.99mm, area 38.6mm2, adj f15,f16,f39,f41
  f41: cylinder r=17mm len=12mm, axis (0,1,0), area 15.8mm2, adj f15,f16,f37,f40
  f42: extruded ~12x2.32mm, area 38.6mm2, adj f15,f16,f43,f46
  f43: plane 12x1.52mm, normal (0.31,0,0.95), area 19.1mm2, adj f10,f15,f16,f42
  f44: plane 12x1.38mm, normal (-0.5,0,-0.87), area 19.1mm2, adj f9,f15,f16,f45
  f45: extruded ~12x3.15mm, area 38.6mm2, adj f15,f16,f44,f46
  f46: cylinder r=17mm len=12mm, axis (0,1,0), area 15.8mm2, adj f15,f16,f42,f45
  f47: extruded ~12x2.91mm, area 38.6mm2, adj f15,f16,f48,f51
  f48: plane 12x1.19mm, normal (0.67,0,0.74), area 19.1mm2, adj f9,f15,f16,f47
  f49: plane 12x1.29mm, normal (-0.81,0,-0.59), area 19.1mm2, adj f8,f15,f16,f50
  f50: extruded ~12x2.77mm, area 38.6mm2, adj f15,f16,f49,f51
  f51: cylinder r=17mm len=12mm, axis (0,1,0), area 15.8mm2, adj f15,f16,f47,f50
  f52: extruded ~12x3.16mm, area 38.6mm2, adj f15,f16,f53,f56
  f53: plane 12x1.46mm, normal (0.91,0,0.41), area 19.1mm2, adj f8,f15,f16,f52
  f54: plane 12x1.56mm, normal (-0.98,0,-0.21), area 19.1mm2, adj f7,f15,f16,f55
  f55: extruded ~12x2.53mm, area 38.6mm2, adj f15,f16,f54,f56
  f56: cylinder r=17mm len=12mm, axis (0,1,0), area 15.8mm2, adj f15,f16,f52,f55
  f57: extruded ~12x2.87mm, area 38.6mm2, adj f15,f16,f58,f61
  f58: plane 12x1.6mm, normal (1,0,0), area 19.1mm2, adj f7,f15,f16,f57
  f59: plane 12x1.56mm, normal (-0.98,0,0.21), area 19.1mm2, adj f6,f15,f16,f60
  f60: extruded ~12x3.08mm, area 38.6mm2, adj f15,f16,f59,f61
  f61: cylinder r=17mm len=12mm, axis (0,1,0), area 15.8mm2, adj f15,f16,f57,f60
  f62: extruded ~12x2.38mm, area 38.6mm2, adj f15,f16,f63,f66
  f63: plane 12x1.46mm, normal (0.91,0,-0.41), area 19.1mm2, adj f6,f15,f16,f62
  f64: plane 12x1.29mm, normal (-0.81,0,0.59), area 19.1mm2, adj f5,f15,f16,f65
  f65: extruded ~12x3.1mm, area 38.6mm2, adj f15,f16,f64,f66
  f66: cylinder r=17mm len=12mm, axis (0,1,0), area 15.8mm2, adj f15,f16,f62,f65
  f67: extruded ~12x3.02mm, area 38.6mm2, adj f15,f16,f68,f71
  f68: plane 12x1.19mm, normal (0.67,0,-0.74), area 19.1mm2, adj f5,f15,f16,f67
  f69: plane 12x1.38mm, normal (-0.5,0,0.87), area 19.1mm2, adj f4,f15,f16,f70
  f70: extruded ~12x2.59mm, area 38.6mm2, adj f15,f16,f69,f71
  f71: cylinder r=17mm len=12mm, axis (0,1,0), area 15.8mm2, adj f15,f16,f67,f70
  f72: extruded ~12x3.14mm, area 38.6mm2, adj f15,f16,f73,f76
  f73: plane 12x1.52mm, normal (0.31,0,-0.95), area 19.1mm2, adj f4,f15,f16,f72
  f74: plane 12x1.59mm, normal (-0.1,0,0.99), area 19.1mm2, adj f3,f15,f16,f75
  f75: extruded ~12x2.71mm, area 38.6mm2, adj f15,f16,f74,f76
  f76: cylinder r=17mm len=12mm, axis (0,1,0), area 15.8mm2, adj f15,f16,f72,f75
  f77: extruded ~12x2.71mm, area 38.6mm2, adj f15,f16,f78,f81
  f78: plane 12x1.59mm, normal (-0.1,0,-0.99), area 19.1mm2, adj f3,f15,f16,f77
  f79: plane 12x1.52mm, normal (0.31,0,0.95), area 19.1mm2, adj f2,f15,f16,f80
  f80: extruded ~12x3.14mm, area 38.6mm2, adj f15,f16,f79,f81
  f81: cylinder r=17mm len=12mm, axis (0,1,0), area 15.8mm2, adj f15,f16,f77,f80
  f82: extruded ~12x2.59mm, area 38.6mm2, adj f15,f16,f83,f86
  f83: plane 12x1.38mm, normal (-0.5,0,-0.87), area 19.1mm2, adj f2,f15,f16,f82
  f84: plane 12x1.19mm, normal (0.67,0,0.74), area 19.1mm2, adj f1,f15,f16,f85
  f85: extruded ~12x3.02mm, area 38.6mm2, adj f15,f16,f84,f86
  f86: cylinder r=17mm len=12mm, axis (0,1,0), area 15.8mm2, adj f15,f16,f82,f85
  f87: extruded ~12x3.1mm, area 38.6mm2, adj f15,f16,f88,f91
  f88: plane 12x1.29mm, normal (-0.81,0,-0.59), area 19.1mm2, adj f1,f15,f16,f87
  f89: plane 12x1.46mm, normal (0.91,0,0.41), area 19.1mm2, adj f0,f15,f16,f90
  f90: extruded ~12x2.38mm, area 38.6mm2, adj f15,f16,f89,f91
  f91: cylinder r=17mm len=12mm, axis (0,1,0), area 15.8mm2, adj f15,f16,f87,f90
  f92: cylinder r=5mm len=12mm, axis (0,1,0), area 377mm2, adj f15,f16
PLACE A rot(axis=(0,1,0),175.3deg) t=(-92.11,11.16,-1.3)mm
PLACE B t=(0.51,55.16,-31.68)mm
PLACE C t=(45.51,55.16,-31.68)mm fixed
PLACE D rot(axis=(0,1,0),156.6deg) t=(-43.99,11.16,-22.06)mm
PLACE E t=(-52.49,55.16,-31.68)mm
PLACE F rot(axis=(0,1,0),136.8deg) t=(-9.88,11.16,-26.73)mm
MATE revolute D.f76 <-> B.f0  axis (0,1,0) through (0.51,5.16,-31.68)mm
MATE revolute F.f41 <-> C.f0  axis (0,1,0) through (45.51,5.16,-31.68)mm
MATE fastened B.f0 <-> E.f1  axis (0,-1,0) through (0.51,-44.84,-31.68)mm
MATE revolute E.f0 <-> A.f114  axis (0,1,0) through (-52.49,5.16,-31.68)mm
MATE planar A.f23 <-> D.f30  axis (0,-1,0) through (-71.04,-0.84,-40.39)mm
MATE fastened C.f0 <-> B.f1  axis (0,1,0) through (45.51,-44.84,-31.68)mm
